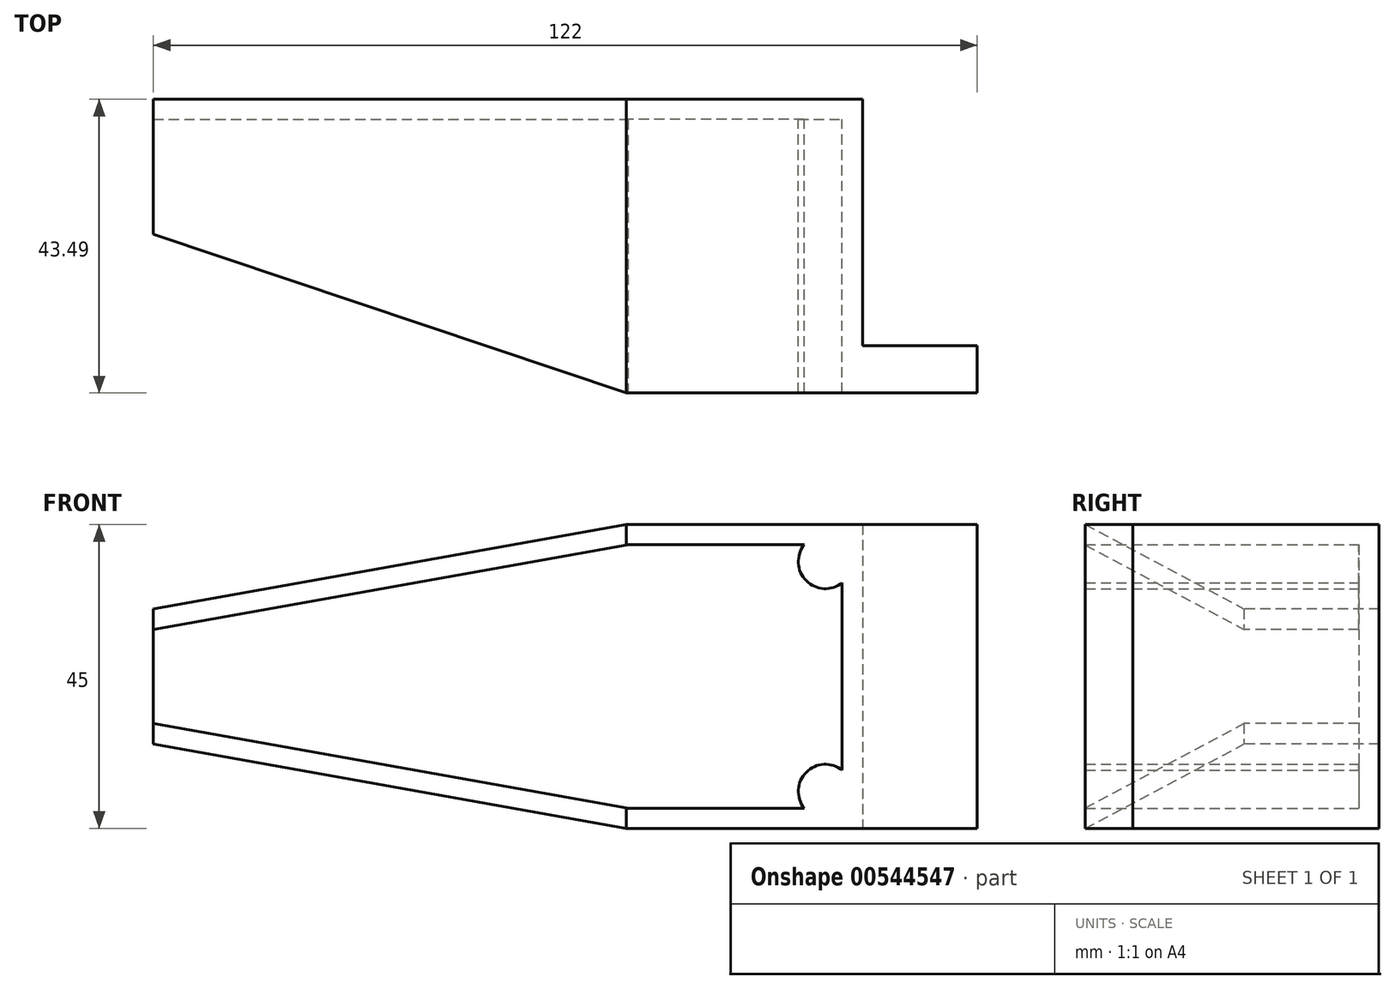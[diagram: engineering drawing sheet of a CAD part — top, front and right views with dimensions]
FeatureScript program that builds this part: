
annotation { "Feature Type Name" : "Feature", "Feature Type Description" : "" }
export const myFeature = defineFeature(function(context is Context, id is Id, definition is map)
    precondition{}
    {
        {
            var Q0;
            Q0=qCreatedBy(makeId("Top.planeOp"),FACE);
            var sketch = newSketch(context, id + "F0", { "sketchPlane" : qUnion([Q0])});
            skLineSegment(sketch, "E0", {"start": v(0, 0) * mm, "end": v(35, 0) * mm});
            skLineSegment(sketch, "E1", {"start": v(35, 0) * mm, "end": v(35, 43.49) * mm});
            skLineSegment(sketch, "E2", {"start": v(35, 43.49) * mm, "end": v(-70, 43.49) * mm});
            skLineSegment(sketch, "E3", {"start": v(-70, 43.49) * mm, "end": v(-70, 23.49) * mm});
            skLineSegment(sketch, "E4", {"start": v(-70, 23.49) * mm, "end": v(0, 0) * mm});
            skSolve(sketch);
        }
        {
            var Q0;
            Q0=makeQuery(id+"F0.imprint","IMPRINT",FACE,{"disambiguationData":[TD([[makeQuery(id+"F0.imprint","IMPRINT",EDGE,{"derivedFrom":sQuery(id+"F0.wireOp",EDGE,"E0")}),1.0]])]});
            extrude(context, id + "F1", {"entities" : qUnion([Q0]), "depth" : 45 * mm, "offsetDistance" : 25 * mm});
        }
        {
            var Q0;
            Q0=qCreatedBy(makeId("Front.planeOp"),FACE);
            var sketch = newSketch(context, id + "F2", { "sketchPlane" : qUnion([Q0])});
            skLineSegment(sketch, "E5", {"start": v(-70, 32.5) * mm, "end": v(0, 45) * mm});
            skLineSegment(sketch, "E6", {"start": v(0, 45) * mm, "end": v(-70, 45) * mm});
            skLineSegment(sketch, "E7", {"start": v(-70, 45) * mm, "end": v(-70, 32.5) * mm});
            skLineSegment(sketch, "E8", {"start": v(-90.8, 22.5) * mm, "end": v(91.4, 22.5) * mm, "construction": true});
            skLineSegment(sketch, "E9.MirrorCS", {"start": v(-70, 12.5) * mm, "end": v(0, 0) * mm});
            skLineSegment(sketch, "E10.MirrorCS", {"start": v(-70, 0) * mm, "end": v(-70, 12.5) * mm});
            skLineSegment(sketch, "E11.MirrorCS", {"start": v(0, 0) * mm, "end": v(-70, 0) * mm});
            skSolve(sketch);
        }
        {
            var Q0;
            Q0 = qSketchRegion(id + "F2", true);
            extrude(context, id + "F3", {"entities" : qUnion([Q0]), "operationType" : NewBodyOperationType.REMOVE, "endBound" : BoundingType.THROUGH_ALL, "oppositeDirection" : true, "depth" : 25 * mm, "offsetDistance" : 25 * mm});
        }
        {
            var Q0;
            Q0=makeQuery(id+"F1.opExtrude","SWEPT_FACE",FACE,{"disambiguationData":[OSD([sQuery(id+"F0.wireOp",EDGE,"E0")])]});
            var Q1;
            Q1=makeQuery(id+"F1.opExtrude","SWEPT_FACE",FACE,{"disambiguationData":[OSD([sQuery(id+"F0.wireOp",EDGE,"E4")])]});
            var Q2;
            Q2=makeQuery(id+"F1.opExtrude","SWEPT_FACE",FACE,{"disambiguationData":[OSD([sQuery(id+"F0.wireOp",EDGE,"E3")])]});
            shell(context, id + "F4", {"entities" : qUnion([Q0, Q1, Q2]), "thickness" : 3 * mm});
        }
        {
            var Q0;
            Q0=qCreatedBy(makeId("Top.planeOp"),FACE);
            var sketch = newSketch(context, id + "F5", { "sketchPlane" : qUnion([Q0])});
            skLineSegment(sketch, "E12.bottom", {"start": v(35, 0) * mm, "end": v(52, 0) * mm});
            skLineSegment(sketch, "E12.top", {"start": v(35, 7) * mm, "end": v(52, 7) * mm});
            skLineSegment(sketch, "E12.left", {"start": v(35, 0) * mm, "end": v(35, 7) * mm});
            skLineSegment(sketch, "E12.right", {"start": v(52, 0) * mm, "end": v(52, 7) * mm});
            skSolve(sketch);
        }
        {
            var Q0;
            Q0 = qSketchRegion(id + "F5", true);
            var Q1;
            Q1=makeQuery(id+"F1.opExtrude","CAP_FACE",FACE,{"disambiguationData":[OSD([sQuery(id+"F0.wireOp",EDGE,"E0"),sQuery(id+"F0.wireOp",EDGE,"E1"),sQuery(id+"F0.wireOp",EDGE,"E2"),sQuery(id+"F0.wireOp",EDGE,"E3"),sQuery(id+"F0.wireOp",EDGE,"E4")])],"isStart":false});
            extrude(context, id + "F6", {"entities" : qUnion([Q0]), "operationType" : NewBodyOperationType.ADD, "endBound" : BoundingType.UP_TO_SURFACE, "depth" : 25 * mm, "endBoundEntityFace" : qUnion([Q1]), "offsetDistance" : 25 * mm});
        }
        {
            var Q0;
            Q0=makeQuery(id+"F4.opShell","OFFSET_FACE",FACE,{"disambiguationData":[OSD([sQuery(id+"F0.wireOp",EDGE,"E2")])]});
            var sketch = newSketch(context, id + "F7", { "sketchPlane" : qUnion([Q0])});
            skCircle(sketch, "E13", {"center": v(-50, 30.5) * mm, "radius": 4 * mm});
            skCircle(sketch, "E14", {"center": v(-50, 14.5) * mm, "radius": 4 * mm});
            skCircle(sketch, "E15", {"center": v(29.5, 5.5) * mm, "radius": 4 * mm});
            skCircle(sketch, "E16", {"center": v(29.5, 39.5) * mm, "radius": 4 * mm});
            skSolve(sketch);
        }
        {
            var Q0;
            {var subQ0=sQuery(id+"F7.wireOp",EDGE,"E13");var subQ1=makeQuery(id+"F4.opShell","OFFSET_EDGE",EDGE,{"disambiguationData":[OSD([sQuery(id+"F0.wireOp",EDGE,"E2"),sQuery(id+"F2.wireOp",EDGE,"E5")])]});var subQ2=makeQuery(id+"F7.imprint","INTERSECT",VERTEX,{"disambiguationData":[OD(0.0)],"derivedFrom":[subQ1,subQ0]});Q0=makeQuery(id+"F7.imprint","IMPRINT",FACE,{"disambiguationData":[TD([[makeQuery(id+"F7.imprint","IMPRINT",EDGE,{"disambiguationData":[TD([[subQ2,-1.0]])],"derivedFrom":subQ0}),1.0]])]});}
            var Q1;
            {var subQ0=sQuery(id+"F7.wireOp",EDGE,"E14");var subQ1=makeQuery(id+"F4.opShell","OFFSET_EDGE",EDGE,{"disambiguationData":[OSD([sQuery(id+"F0.wireOp",EDGE,"E2"),sQuery(id+"F2.wireOp",EDGE,"E9.MirrorCS")])]});var subQ2=makeQuery(id+"F7.imprint","INTERSECT",VERTEX,{"disambiguationData":[OD(0.0)],"derivedFrom":[subQ1,subQ0]});Q1=makeQuery(id+"F7.imprint","IMPRINT",FACE,{"disambiguationData":[TD([[makeQuery(id+"F7.imprint","IMPRINT",EDGE,{"disambiguationData":[TD([[subQ2,1.0]])],"derivedFrom":subQ0}),1.0]])]});}
            var Q2;
            Q2=makeQuery(id+"F4.opShell","OFFSET_FACE",FACE,{"disambiguationData":[OSD([sQuery(id+"F0.wireOp",EDGE,"E4")])]});
            extrude(context, id + "F8", {"entities" : qUnion([Q0, Q1]), "operationType" : NewBodyOperationType.ADD, "endBound" : BoundingType.UP_TO_SURFACE, "depth" : 25 * mm, "endBoundEntityFace" : qUnion([Q2]), "offsetDistance" : 25 * mm});
        }
        {
            var Q0;
            {var subQ0=sQuery(id+"F7.wireOp",EDGE,"E16");var subQ1=sQuery(id+"F0.wireOp",EDGE,"E2");var subQ4=makeQuery(id+"F4.opShell","OFFSET_EDGE",EDGE,{"disambiguationData":[OSD([subQ1]),TDD([makeQuery(id+"F1.opExtrude","CAP_EDGE",EDGE,{"disambiguationData":[OSD([subQ1])],"isStart":false})])]});var subQ5=makeQuery(id+"F7.imprint","INTERSECT",VERTEX,{"derivedFrom":[subQ4,subQ0]});Q0=makeQuery(id+"F7.imprint","IMPRINT",FACE,{"disambiguationData":[TD([[makeQuery(id+"F7.imprint","IMPRINT",EDGE,{"disambiguationData":[TD([[subQ5,-1.0]])],"derivedFrom":subQ0}),1.0]])]});}
            var Q1;
            {var subQ0=sQuery(id+"F7.wireOp",EDGE,"E15");var subQ1=sQuery(id+"F0.wireOp",EDGE,"E2");var subQ4=makeQuery(id+"F4.opShell","OFFSET_EDGE",EDGE,{"disambiguationData":[OSD([subQ1]),TDD([makeQuery(id+"F1.opExtrude","CAP_EDGE",EDGE,{"disambiguationData":[OSD([subQ1])],"isStart":true})])]});var subQ5=makeQuery(id+"F7.imprint","INTERSECT",VERTEX,{"derivedFrom":[subQ4,subQ0]});Q1=makeQuery(id+"F7.imprint","IMPRINT",FACE,{"disambiguationData":[TD([[makeQuery(id+"F7.imprint","IMPRINT",EDGE,{"disambiguationData":[TD([[subQ5,1.0]])],"derivedFrom":subQ0}),1.0]])]});}
            var Q2;
            Q2=makeQuery(id+"F6.boolean.opBoolean","MERGE",FACE,{"derivedFrom":[makeQuery(id+"F1.opExtrude","SWEPT_FACE",FACE,{"disambiguationData":[OSD([sQuery(id+"F0.wireOp",EDGE,"E0")])]}),makeQuery(id+"F6.opExtrude","SWEPT_FACE",FACE,{"disambiguationData":[OSD([sQuery(id+"F5.wireOp",EDGE,"E12.bottom")])]})]});
            extrude(context, id + "F9", {"entities" : qUnion([Q0, Q1]), "operationType" : NewBodyOperationType.ADD, "endBound" : BoundingType.UP_TO_SURFACE, "depth" : 25 * mm, "endBoundEntityFace" : qUnion([Q2]), "offsetDistance" : 25 * mm});
        }
    });
